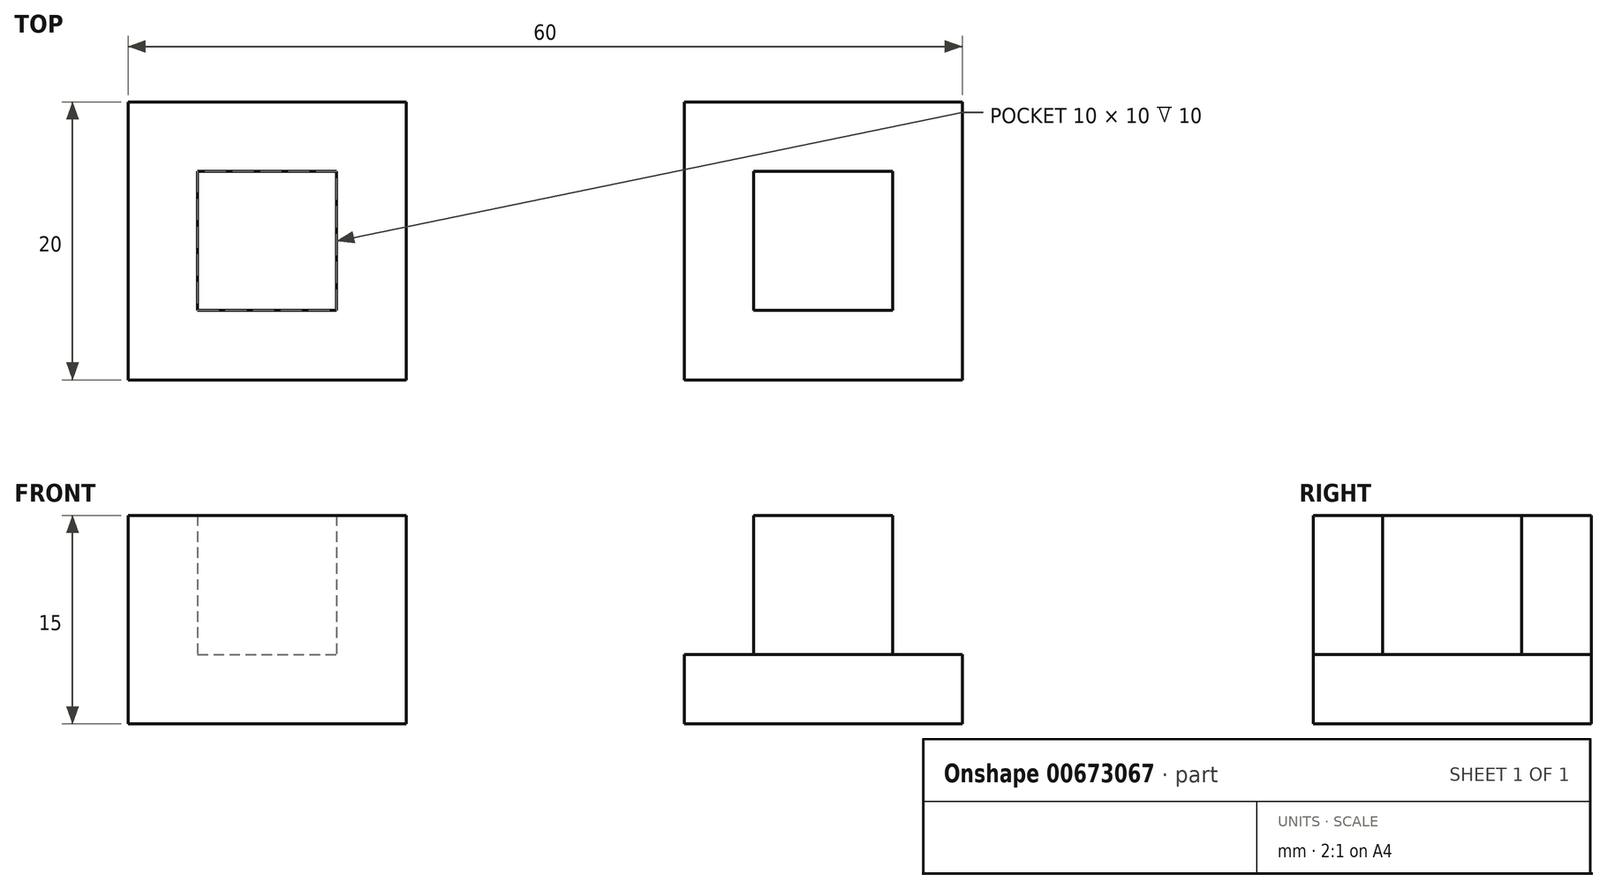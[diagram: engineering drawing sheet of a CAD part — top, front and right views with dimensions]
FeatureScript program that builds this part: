
annotation { "Feature Type Name" : "Feature", "Feature Type Description" : "" }
export const myFeature = defineFeature(function(context is Context, id is Id, definition is map)
    precondition{}
    {
        {
            var Q0;
            Q0=qCreatedBy(makeId("Top.planeOp"),FACE);
            var sketch = newSketch(context, id + "F0", { "sketchPlane" : qUnion([Q0])});
            skLineSegment(sketch, "E0.bottom", {"start": v(10, -10) * mm, "end": v(-10, -10) * mm});
            skLineSegment(sketch, "E0.top", {"start": v(10, 10) * mm, "end": v(-10, 10) * mm});
            skLineSegment(sketch, "E0.left", {"start": v(10, -10) * mm, "end": v(10, 10) * mm});
            skLineSegment(sketch, "E0.right", {"start": v(-10, -10) * mm, "end": v(-10, 10) * mm});
            skPoint(sketch, "E0.middle", {"position": v(0, 0) * mm});
            skLineSegment(sketch, "E1.bottom", {"start": v(5, -5) * mm, "end": v(-5, -5) * mm});
            skLineSegment(sketch, "E1.top", {"start": v(5, 5) * mm, "end": v(-5, 5) * mm});
            skLineSegment(sketch, "E1.left", {"start": v(5, -5) * mm, "end": v(5, 5) * mm});
            skLineSegment(sketch, "E1.right", {"start": v(-5, -5) * mm, "end": v(-5, 5) * mm});
            skSolve(sketch);
        }
        {
            var Q0;
            Q0=makeQuery(id+"F0.imprint","IMPRINT",FACE,{"disambiguationData":[TD([[makeQuery(id+"F0.imprint","IMPRINT",EDGE,{"derivedFrom":sQuery(id+"F0.wireOp",EDGE,"E0.bottom")}),-1.0]])]});
            var Q1;
            Q1=makeQuery(id+"F0.imprint","IMPRINT",FACE,{"disambiguationData":[TD([[makeQuery(id+"F0.imprint","IMPRINT",EDGE,{"derivedFrom":sQuery(id+"F0.wireOp",EDGE,"E1.bottom")}),-1.0]])]});
            extrude(context, id + "F1", {"entities" : qUnion([Q0, Q1]), "depth" : 5 * mm, "offsetDistance" : 25 * mm});
        }
        {
            var Q0;
            Q0=makeQuery(id+"F0.imprint","IMPRINT",FACE,{"disambiguationData":[TD([[makeQuery(id+"F0.imprint","IMPRINT",EDGE,{"derivedFrom":sQuery(id+"F0.wireOp",EDGE,"E1.bottom")}),-1.0]])]});
            extrude(context, id + "F2", {"entities" : qUnion([Q0]), "operationType" : NewBodyOperationType.ADD, "depth" : 15 * mm, "offsetDistance" : 25 * mm});
        }
        {
            var Q0;
            Q0=makeQuery(id+"F1.opExtrude","SWEPT_BODY",BODY,{"disambiguationData":[OSD([sQuery(id+"F0.wireOp",EDGE,"E0.bottom"),sQuery(id+"F0.wireOp",EDGE,"E0.top"),sQuery(id+"F0.wireOp",EDGE,"E0.left"),sQuery(id+"F0.wireOp",EDGE,"E0.right")])]});
            transform(context, id + "F3", {"entities" : qUnion([Q0]), "transformType" : TransformType.TRANSLATION_3D, "dx" : 30 * mm, "dy" : 0 * mm, "dz" : 0 * mm, "makeCopy" : false});
        }
        {
            var Q0;
            Q0 = qSketchRegion(id + "F0", true);
            extrude(context, id + "F4", {"entities" : qUnion([Q0]), "oppositeDirection" : true, "depth" : 15 * mm, "offsetDistance" : 25 * mm});
        }
        {
            var Q0;
            Q0=makeQuery(id+"F0.imprint","IMPRINT",FACE,{"disambiguationData":[TD([[makeQuery(id+"F0.imprint","IMPRINT",EDGE,{"derivedFrom":sQuery(id+"F0.wireOp",EDGE,"E1.bottom")}),-1.0]])]});
            extrude(context, id + "F5", {"entities" : qUnion([Q0]), "operationType" : NewBodyOperationType.ADD, "oppositeDirection" : true, "depth" : 5 * mm, "offsetDistance" : 25 * mm});
        }
        {
            var Q0;
            Q0=makeQuery(id+"F4.opExtrude","SWEPT_BODY",BODY,{"disambiguationData":[OSD([sQuery(id+"F0.wireOp",EDGE,"E0.bottom"),sQuery(id+"F0.wireOp",EDGE,"E0.top"),sQuery(id+"F0.wireOp",EDGE,"E0.left"),sQuery(id+"F0.wireOp",EDGE,"E0.right"),sQuery(id+"F0.wireOp",EDGE,"E1.bottom"),sQuery(id+"F0.wireOp",EDGE,"E1.top"),sQuery(id+"F0.wireOp",EDGE,"E1.left"),sQuery(id+"F0.wireOp",EDGE,"E1.right")])]});
            var Q1;
            Q1=sQuery(id+"F0.wireOp",EDGE,"E1.right");
            transform(context, id + "F6", {"entities" : qUnion([Q0]), "transformType" : TransformType.ROTATION, "transformAxis" : qUnion([Q1]), "angle" : 180 * degree, "oppositeDirection" : true, "makeCopy" : false});
        }
    });
